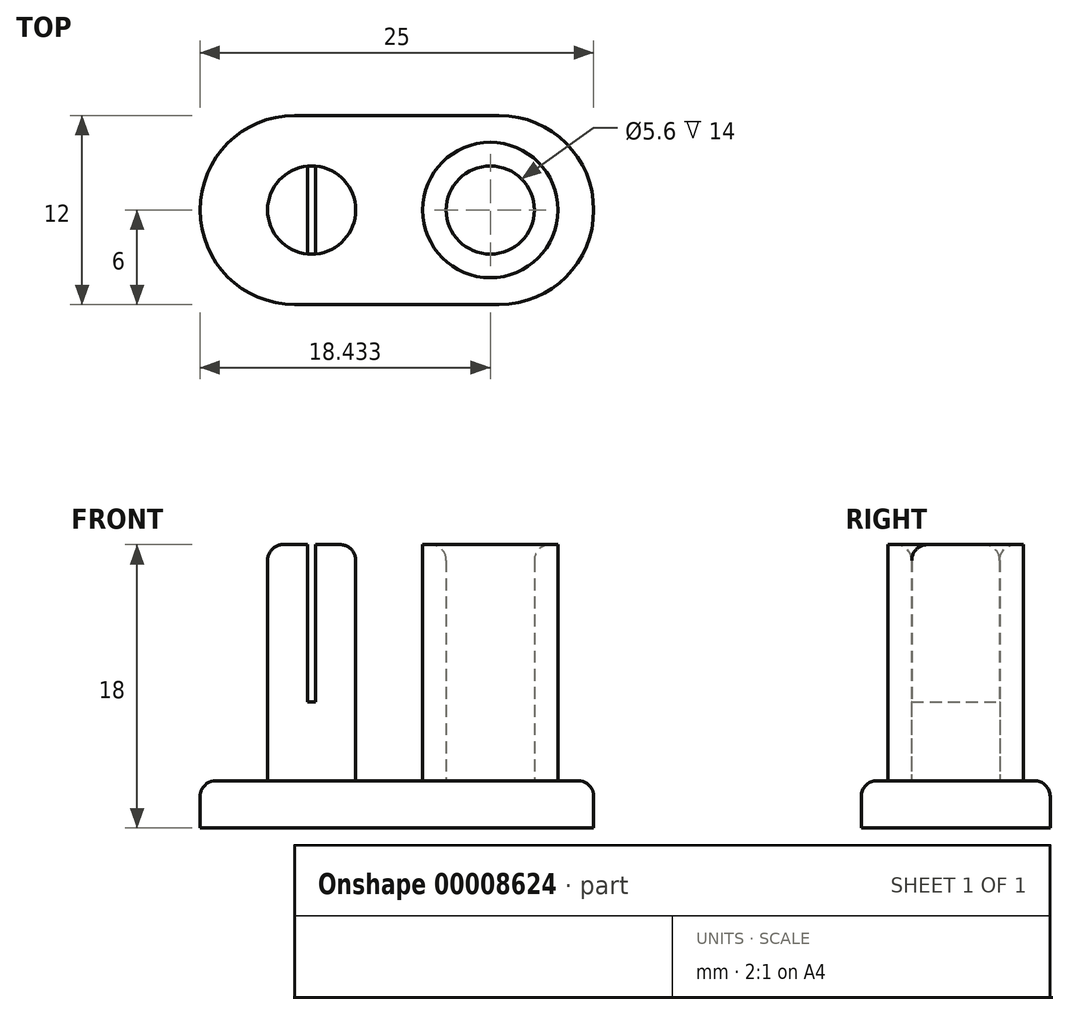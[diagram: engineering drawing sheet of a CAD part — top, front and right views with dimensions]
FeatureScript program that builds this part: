
annotation { "Feature Type Name" : "Feature", "Feature Type Description" : "" }
export const myFeature = defineFeature(function(context is Context, id is Id, definition is map)
    precondition{}
    {
        {
            var Q0;
            Q0=qCreatedBy(makeId("Top.planeOp"),FACE);
            var sketch = newSketch(context, id + "F0", { "sketchPlane" : qUnion([Q0])});
            skLineSegment(sketch, "E0.rect.bottom", {"start": v(6.5, -6) * mm, "end": v(-6.5, -6) * mm});
            skLineSegment(sketch, "E0.rect.top", {"start": v(6.5, 6) * mm, "end": v(-6.5, 6) * mm});
            skLineSegment(sketch, "E0.rect.left", {"start": v(6.5, -6) * mm, "end": v(6.5, 6) * mm});
            skLineSegment(sketch, "E0.rect.right", {"start": v(-6.5, -6) * mm, "end": v(-6.5, 6) * mm});
            skPoint(sketch, "E0.rect.middle", {"position": v(0, 0) * mm});
            skArc(sketch, "E1", {"start": v(-6.5, 6) * mm, "mid": v(-12.5, 0) * mm, "end": v(-6.5, -6) * mm});
            skArc(sketch, "E2", {"start": v(6.5, -6) * mm, "mid": v(12.5, 0) * mm, "end": v(6.5, 6) * mm});
            skSolve(sketch);
        }
        {
            var Q0;
            Q0 = qSketchRegion(id + "F0", true);
            extrude(context, id + "F1", {"entities" : qUnion([Q0]), "depth" : 3 * mm});
        }
        {
            var Q0;
            Q0=makeQuery(id+"F1.opExtrude","CAP_FACE",FACE,{"disambiguationData":[OSD([sQuery(id+"F0.wireOp",EDGE,"E0.rect.bottom"),sQuery(id+"F0.wireOp",EDGE,"E0.rect.top"),sQuery(id+"F0.wireOp",EDGE,"E1"),sQuery(id+"F0.wireOp",EDGE,"E2")])],"isStart":false});
            var sketch = newSketch(context, id + "F2", { "sketchPlane" : qUnion([Q0])});
            skCircle(sketch, "E3", {"center": v(-5.41, 0) * mm, "radius": 2.8 * mm});
            skCircle(sketch, "E4", {"center": v(5.93, 0) * mm, "radius": 2.8 * mm});
            skCircle(sketch, "E5.0", {"center": v(5.93, 0) * mm, "radius": 4.3 * mm});
            skSolve(sketch);
        }
        {
            var Q0;
            Q0=makeQuery(id+"F2.imprint","IMPRINT",FACE,{"disambiguationData":[TD([[makeQuery(id+"F2.imprint","IMPRINT",EDGE,{"derivedFrom":sQuery(id+"F2.wireOp",EDGE,"E3")}),1.0]])]});
            var Q1;
            Q1=makeQuery(id+"F2.imprint","IMPRINT",FACE,{"disambiguationData":[TD([[makeQuery(id+"F2.imprint","IMPRINT",EDGE,{"derivedFrom":sQuery(id+"F2.wireOp",EDGE,"E4")}),-1.0]])]});
            extrude(context, id + "F3", {"entities" : qUnion([Q0, Q1]), "operationType" : NewBodyOperationType.ADD, "depth" : 15 * mm});
        }
        {
            var Q0;
            Q0=makeQuery(id+"F3.opExtrude","CAP_FACE",FACE,{"disambiguationData":[OSD([sQuery(id+"F2.wireOp",EDGE,"E3")])],"isStart":false});
            var sketch = newSketch(context, id + "F4", { "sketchPlane" : qUnion([Q0])});
            skLineSegment(sketch, "E6.rect.bottom", {"start": v(-5.16, -3) * mm, "end": v(-5.66, -3) * mm});
            skLineSegment(sketch, "E6.rect.top", {"start": v(-5.16, 3) * mm, "end": v(-5.66, 3) * mm});
            skLineSegment(sketch, "E6.rect.left", {"start": v(-5.16, -3) * mm, "end": v(-5.16, 3) * mm});
            skLineSegment(sketch, "E6.rect.right", {"start": v(-5.66, -3) * mm, "end": v(-5.66, 3) * mm});
            skPoint(sketch, "E6.rect.middle", {"position": v(-5.41, 0) * mm});
            skSolve(sketch);
        }
        {
            var Q0;
            {var subQ5=sQuery(id+"F4.wireOp",EDGE,"E6.rect.top");Q0=makeQuery(id+"F4.imprint","IMPRINT",FACE,{"disambiguationData":[TD([[makeQuery(id+"F4.imprint","IMPRINT",EDGE,{"derivedFrom":subQ5}),1.0]])]});}
            var Q1;
            {var subQ0=makeQuery(id+"F3.opExtrude","CAP_EDGE",EDGE,{"disambiguationData":[OSD([sQuery(id+"F2.wireOp",EDGE,"E3")])],"isStart":false});var subQ3=sQuery(id+"F4.wireOp",EDGE,"E6.rect.left");var subQ6=makeQuery(id+"F4.imprint","INTERSECT",VERTEX,{"disambiguationData":[OD(0.0)],"derivedFrom":[subQ0,subQ3]});Q1=makeQuery(id+"F4.imprint","IMPRINT",FACE,{"disambiguationData":[TD([[makeQuery(id+"F4.imprint","IMPRINT",EDGE,{"disambiguationData":[TD([[subQ6,-1.0]])],"derivedFrom":subQ3}),1.0]])]});}
            var Q2;
            {var subQ5=sQuery(id+"F4.wireOp",EDGE,"E6.rect.bottom");Q2=makeQuery(id+"F4.imprint","IMPRINT",FACE,{"disambiguationData":[TD([[makeQuery(id+"F4.imprint","IMPRINT",EDGE,{"derivedFrom":subQ5}),-1.0]])]});}
            var Q3;
            {var subQ0=sQuery(id+"F0.wireOp",EDGE,"E0.rect.bottom");var subQ1=sQuery(id+"F0.wireOp",EDGE,"E0.rect.top");var subQ2=sQuery(id+"F0.wireOp",EDGE,"E1");var subQ3=sQuery(id+"F0.wireOp",EDGE,"E2");Q3=makeQuery(id+"F3.boolean.opBoolean","SPLIT",FACE,{"disambiguationData":[TD([makeQuery(id+"F1.opExtrude","SWEPT_FACE",FACE,{"disambiguationData":[OSD([subQ0])]})])],"derivedFrom":makeQuery(id+"F1.opExtrude","CAP_FACE",FACE,{"disambiguationData":[OSD([subQ0,subQ1,subQ2,subQ3])],"isStart":false})});}
            extrude(context, id + "F5", {"entities" : qUnion([Q0, Q1, Q2]), "operationType" : NewBodyOperationType.REMOVE, "oppositeDirection" : true, "endBoundEntity" : qUnion([Q3]), "depth" : 10 * mm});
        }
        {
            var Q0;
            Q0=makeQuery(id+"F3.opExtrude","CAP_EDGE",EDGE,{"disambiguationData":[OSD([sQuery(id+"F2.wireOp",EDGE,"E4")])],"isStart":false});
            var Q1;
            Q1=makeQuery(id+"F3.opExtrude","CAP_EDGE",EDGE,{"disambiguationData":[OSD([sQuery(id+"F2.wireOp",EDGE,"E5.0")])],"isStart":true});
            var Q2;
            {var subQ0=sQuery(id+"F2.wireOp",EDGE,"E3");var subQ1=sQuery(id+"F4.wireOp",EDGE,"E6.rect.right");Q2=makeQuery(id+"F5.boolean.opBoolean","SPLIT",EDGE,{"disambiguationData":[TD([makeQuery(id+"F5.opExtrude","SWEPT_FACE",FACE,{"disambiguationData":[OSD([subQ1])]})])],"derivedFrom":makeQuery(id+"F3.opExtrude","CAP_EDGE",EDGE,{"disambiguationData":[OSD([subQ0])],"isStart":true})});}
            var Q3;
            {var subQ0=sQuery(id+"F2.wireOp",EDGE,"E3");var subQ1=sQuery(id+"F4.wireOp",EDGE,"E6.rect.left");Q3=makeQuery(id+"F5.boolean.opBoolean","SPLIT",EDGE,{"disambiguationData":[TD([makeQuery(id+"F5.opExtrude","SWEPT_FACE",FACE,{"disambiguationData":[OSD([subQ1])]})])],"derivedFrom":makeQuery(id+"F3.opExtrude","CAP_EDGE",EDGE,{"disambiguationData":[OSD([subQ0])],"isStart":true})});}
            var Q4;
            {var subQ0=sQuery(id+"F2.wireOp",EDGE,"E3");Q4=makeQuery(id+"F5.boolean.opBoolean","SPLIT",EDGE,{"disambiguationData":[TD([makeQuery(id+"F5.opExtrude","SWEPT_FACE",FACE,{"disambiguationData":[OSD([sQuery(id+"F4.wireOp",EDGE,"E6.rect.right")])]})])],"derivedFrom":makeQuery(id+"F3.opExtrude","CAP_EDGE",EDGE,{"disambiguationData":[OSD([subQ0])],"isStart":false})});}
            var Q5;
            {var subQ0=sQuery(id+"F2.wireOp",EDGE,"E3");Q5=makeQuery(id+"F5.boolean.opBoolean","SPLIT",EDGE,{"disambiguationData":[TD([makeQuery(id+"F5.opExtrude","SWEPT_FACE",FACE,{"disambiguationData":[OSD([sQuery(id+"F4.wireOp",EDGE,"E6.rect.left")])]})])],"derivedFrom":makeQuery(id+"F3.opExtrude","CAP_EDGE",EDGE,{"disambiguationData":[OSD([subQ0])],"isStart":false})});}
            fillet(context, id + "F6", {"entities" : qUnion([Q0, Q1, Q2, Q3, Q4, Q5]), "radius" : 1 * mm, "tangentPropagation" : true, "allowEdgeOverflow" : false});
        }
        {
            var Q0;
            Q0=makeQuery(id+"F1.opExtrude","CAP_EDGE",EDGE,{"disambiguationData":[OSD([sQuery(id+"F0.wireOp",EDGE,"E1")])],"isStart":false});
            var Q1;
            Q1=makeQuery(id+"F1.opExtrude","CAP_EDGE",EDGE,{"disambiguationData":[OSD([sQuery(id+"F0.wireOp",EDGE,"E0.rect.bottom")])],"isStart":false});
            var Q2;
            Q2=makeQuery(id+"F1.opExtrude","CAP_EDGE",EDGE,{"disambiguationData":[OSD([sQuery(id+"F0.wireOp",EDGE,"E2")])],"isStart":false});
            var Q3;
            Q3=makeQuery(id+"F1.opExtrude","CAP_EDGE",EDGE,{"disambiguationData":[OSD([sQuery(id+"F0.wireOp",EDGE,"E0.rect.top")])],"isStart":false});
            fillet(context, id + "F7", {"entities" : qUnion([Q0, Q1, Q2, Q3]), "radius" : 1 * mm, "tangentPropagation" : true, "allowEdgeOverflow" : false});
        }
    });
